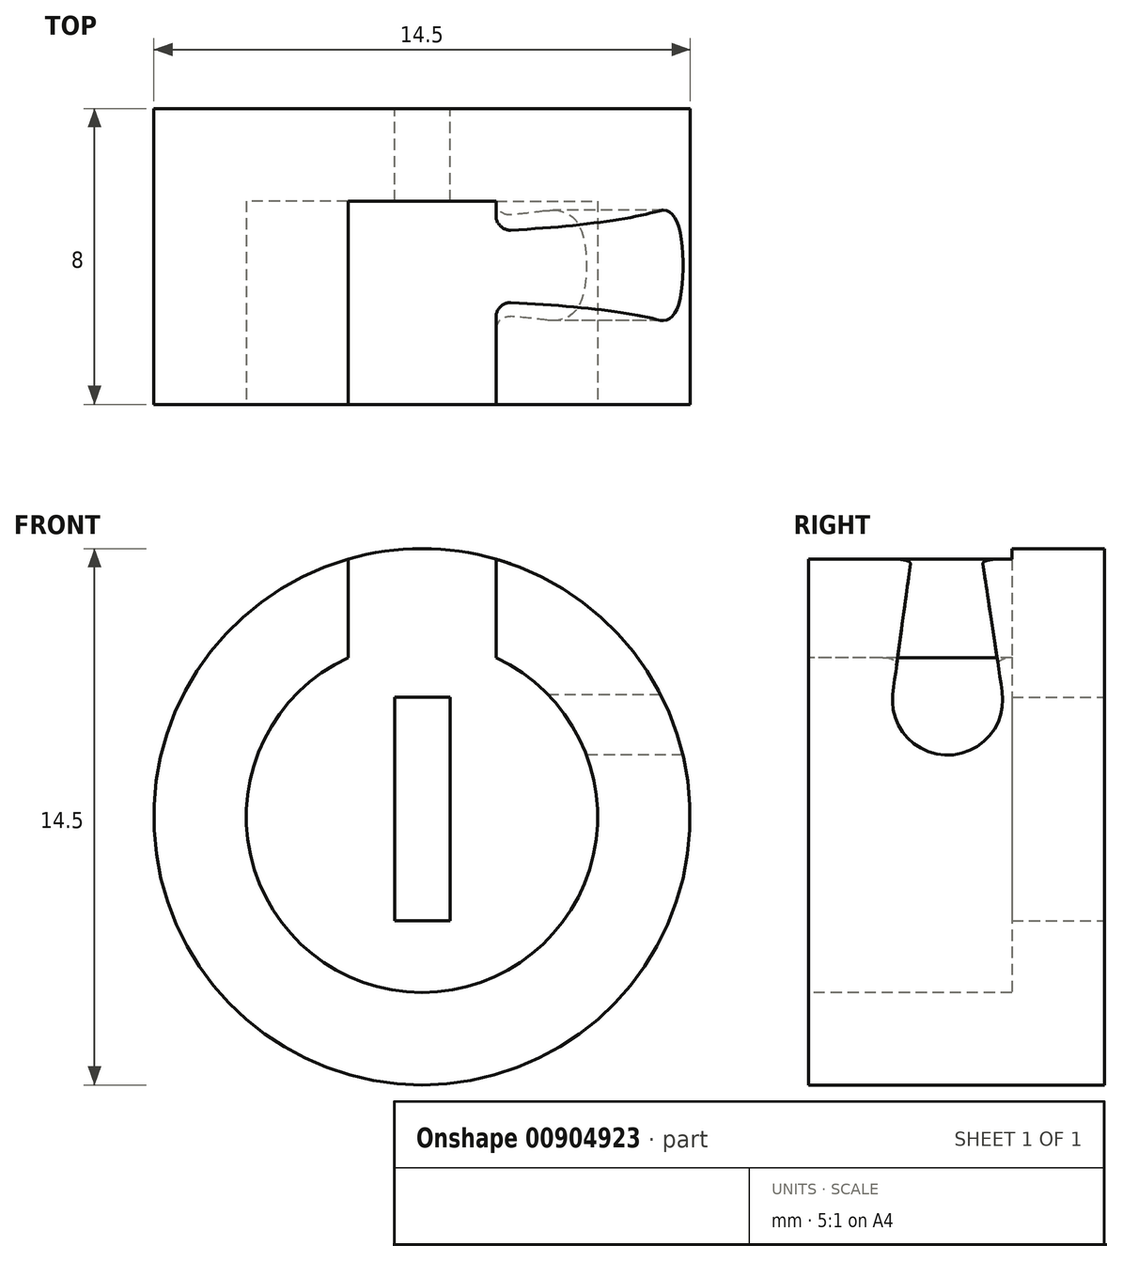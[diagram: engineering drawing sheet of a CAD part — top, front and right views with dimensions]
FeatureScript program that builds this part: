
annotation { "Feature Type Name" : "Feature", "Feature Type Description" : "" }
export const myFeature = defineFeature(function(context is Context, id is Id, definition is map)
    precondition{}
    {
        {
            var Q0;
            Q0=qCreatedBy(makeId("Front.planeOp"),FACE);
            var sketch = newSketch(context, id + "F0", { "sketchPlane" : qUnion([Q0])});
            skCircle(sketch, "E0", {"center": v(0, 0) * mm, "radius": 7.25 * mm});
            skSolve(sketch);
        }
        {
            var Q0;
            Q0 = qSketchRegion(id + "F0", true);
            extrude(context, id + "F1", {"entities" : qUnion([Q0]), "depth" : 8 * mm, "offsetDistance" : 25 * mm});
        }
        {
            var Q0;
            Q0=makeQuery(id+"F1.opExtrude","CAP_FACE",FACE,{"disambiguationData":[OSD([sQuery(id+"F0.wireOp",EDGE,"E0")])],"isStart":false});
            var sketch = newSketch(context, id + "F2", { "sketchPlane" : qUnion([Q0])});
            skCircle(sketch, "E1.0", {"center": v(0, 0) * mm, "radius": 4.75 * mm});
            skSolve(sketch);
        }
        {
            var Q0;
            Q0=makeQuery(id+"F2.imprint","IMPRINT",FACE,{"disambiguationData":[TD([[makeQuery(id+"F2.imprint","IMPRINT",EDGE,{"derivedFrom":sQuery(id+"F2.wireOp",EDGE,"E1.0")}),1.0]])]});
            extrude(context, id + "F3", {"entities" : qUnion([Q0]), "operationType" : NewBodyOperationType.REMOVE, "oppositeDirection" : true, "depth" : 5.5 * mm, "offsetDistance" : 25 * mm});
        }
        {
            var Q0;
            Q0=makeQuery(id+"F2.imprint","IMPRINT",FACE,{"disambiguationData":[TD([[makeQuery(id+"F2.imprint","IMPRINT",EDGE,{"derivedFrom":sQuery(id+"F2.wireOp",EDGE,"E1.0")}),-1.0]])]});
            var sketch = newSketch(context, id + "F4", { "sketchPlane" : qUnion([Q0])});
            skLineSegment(sketch, "E2.bottom", {"start": v(-2, 0) * mm, "end": v(2, 0) * mm});
            skLineSegment(sketch, "E2.top", {"start": v(-2, 9.44) * mm, "end": v(2, 9.44) * mm});
            skLineSegment(sketch, "E2.left", {"start": v(-2, 0) * mm, "end": v(-2, 9.44) * mm});
            skLineSegment(sketch, "E2.right", {"start": v(2, 0) * mm, "end": v(2, 9.44) * mm});
            skSolve(sketch);
        }
        {
            var Q0;
            {var subQ0=sQuery(id+"F4.wireOp",EDGE,"E2.top");Q0=makeQuery(id+"F4.imprint","IMPRINT",FACE,{"disambiguationData":[TD([[makeQuery(id+"F4.imprint","IMPRINT",EDGE,{"derivedFrom":subQ0}),-1.0]])]});}
            var Q1;
            Q1 = qSketchRegion(id + "F4", true);
            var Q2;
            Q2=makeQuery(id+"F3.boolean.opBoolean","COPY",FACE,{"derivedFrom":makeQuery(id+"F3.opExtrude","CAP_FACE",FACE,{"disambiguationData":[OSD([sQuery(id+"F2.wireOp",EDGE,"E1.0")])],"isStart":false})});
            extrude(context, id + "F5", {"entities" : qUnion([Q0, Q1]), "operationType" : NewBodyOperationType.REMOVE, "endBound" : BoundingType.UP_TO_SURFACE, "oppositeDirection" : true, "depth" : 25 * mm, "endBoundEntityFace" : qUnion([Q2]), "offsetDistance" : 25 * mm});
        }
        {
            var Q0;
            Q0=qCreatedBy(makeId("Right.planeOp"),FACE);
            var sketch = newSketch(context, id + "F6", { "sketchPlane" : qUnion([Q0])});
            skLineSegment(sketch, "E3", {"start": v(-5.73, 3.3) * mm, "end": v(-5.09, 7.97) * mm});
            skLineSegment(sketch, "E4.MirrorCS", {"start": v(-2.76, 3.38) * mm, "end": v(-3.46, 8) * mm});
            skLineSegment(sketch, "E5", {"start": v(-5.09, 7.97) * mm, "end": v(-3.46, 8) * mm});
            skArc(sketch, "E6", {"start": v(-5.73, 3.3) * mm, "mid": v(-4.2, 1.67) * mm, "end": v(-2.76, 3.38) * mm});
            skSolve(sketch);
        }
        {
            var Q0;
            Q0 = qSketchRegion(id + "F6", true);
            extrude(context, id + "F7", {"entities" : qUnion([Q0]), "operationType" : NewBodyOperationType.REMOVE, "endBound" : BoundingType.THROUGH_ALL, "depth" : 25 * mm, "offsetDistance" : 25 * mm});
        }
        {
            var Q0;
            Q0=makeQuery(id+"F0.imprint","IMPRINT",FACE,{"disambiguationData":[TD([[makeQuery(id+"F0.imprint","IMPRINT",EDGE,{"derivedFrom":sQuery(id+"F0.wireOp",EDGE,"E0")}),1.0]])]});
            var sketch = newSketch(context, id + "F8", { "sketchPlane" : qUnion([Q0])});
            skLineSegment(sketch, "E7.bottom", {"start": v(0.76, -2.8) * mm, "end": v(-0.74, -2.8) * mm});
            skLineSegment(sketch, "E7.top", {"start": v(0.76, 3.24) * mm, "end": v(-0.74, 3.24) * mm});
            skLineSegment(sketch, "E7.left", {"start": v(0.76, -2.8) * mm, "end": v(0.76, 3.24) * mm});
            skLineSegment(sketch, "E7.right", {"start": v(-0.74, -2.8) * mm, "end": v(-0.74, 3.24) * mm});
            skSolve(sketch);
        }
        {
            var Q0;
            Q0 = qSketchRegion(id + "F8", true);
            extrude(context, id + "F9", {"entities" : qUnion([Q0]), "operationType" : NewBodyOperationType.REMOVE, "depth" : 25 * mm, "offsetDistance" : 25 * mm});
        }
        {
            var Q0;
            Q0=makeQuery(id+"F7.boolean.opBoolean","INTERSECT",EDGE,{"derivedFrom":[makeQuery(id+"F5.boolean.opBoolean","COPY",FACE,{"derivedFrom":makeQuery(id+"F5.opExtrude","SWEPT_FACE",FACE,{"disambiguationData":[OSD([sQuery(id+"F4.wireOp",EDGE,"E2.right")])]})}),makeQuery(id+"F7.opExtrude","SWEPT_FACE",FACE,{"disambiguationData":[OSD([sQuery(id+"F6.wireOp",EDGE,"E4.MirrorCS")])]})]});
            var Q1;
            Q1=makeQuery(id+"F7.boolean.opBoolean","INTERSECT",EDGE,{"derivedFrom":[makeQuery(id+"F5.boolean.opBoolean","COPY",FACE,{"derivedFrom":makeQuery(id+"F5.opExtrude","SWEPT_FACE",FACE,{"disambiguationData":[OSD([sQuery(id+"F4.wireOp",EDGE,"E2.right")])]})}),makeQuery(id+"F7.opExtrude","SWEPT_FACE",FACE,{"disambiguationData":[OSD([sQuery(id+"F6.wireOp",EDGE,"E3")])]})]});
            fillet(context, id + "F10", {"entities" : qUnion([Q0, Q1]), "tangentPropagation" : true, "radius" : 0.4 * mm, "defaultsChanged" : true, "vertexSettings" : [], "allowEdgeOverflow" : false});
        }
    });
